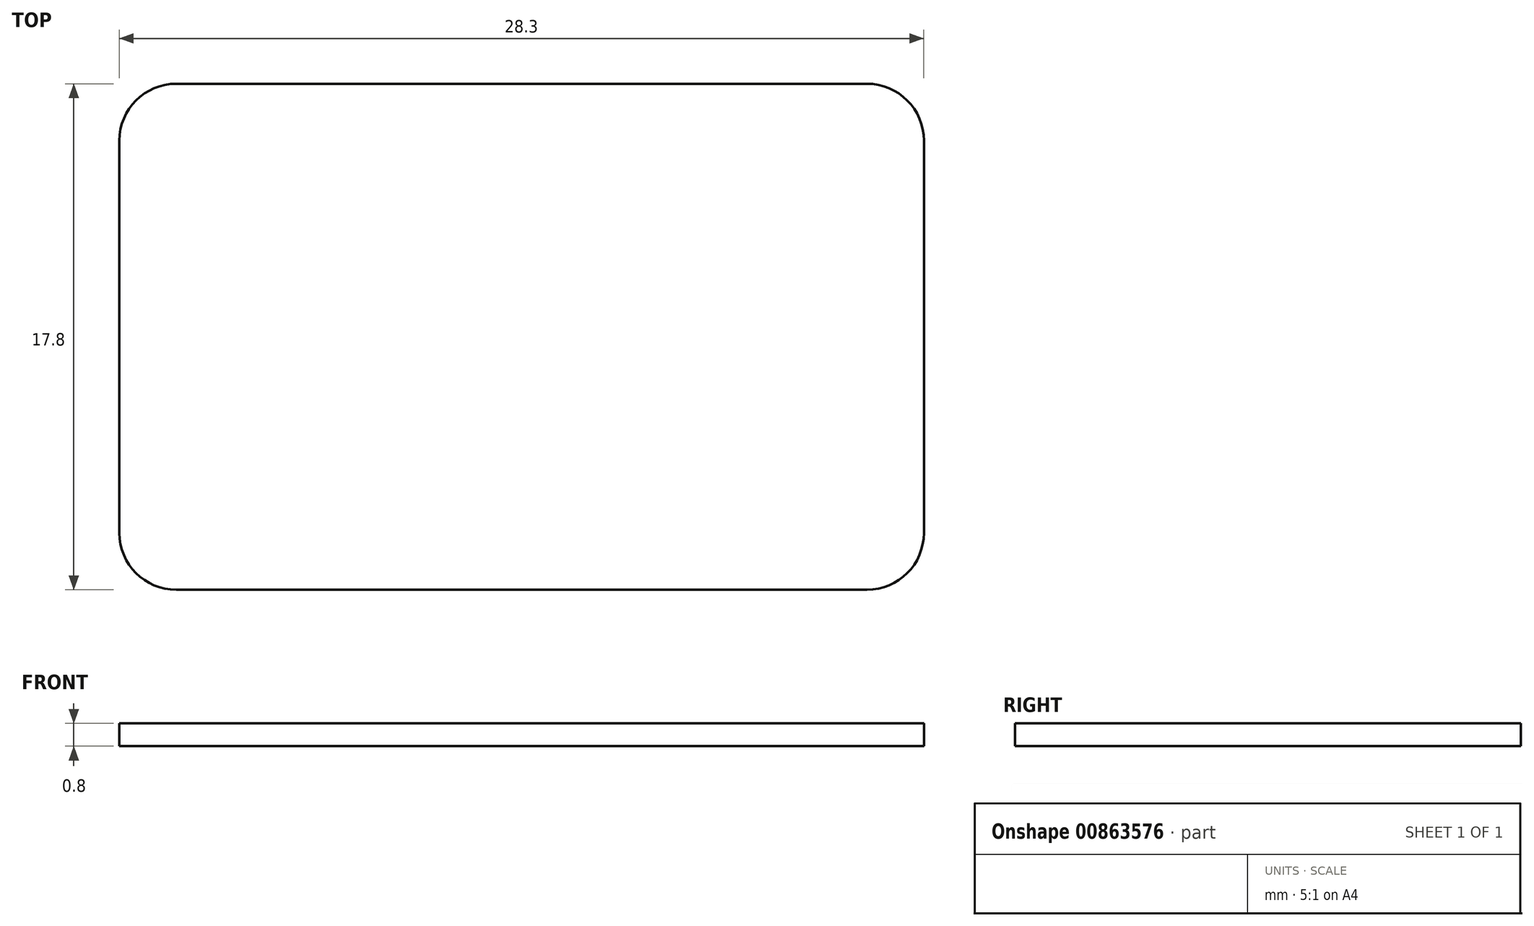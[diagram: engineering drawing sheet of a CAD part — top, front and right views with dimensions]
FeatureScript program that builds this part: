
annotation { "Feature Type Name" : "Feature", "Feature Type Description" : "" }
export const myFeature = defineFeature(function(context is Context, id is Id, definition is map)
    precondition{}
    {
        {
            var Q0;
            Q0=qCreatedBy(makeId("Top.planeOp"),FACE);
            var sketch = newSketch(context, id + "F0", { "sketchPlane" : qUnion([Q0])});
            skLineSegment(sketch, "E0.bottom", {"start": v(-21.54, 8.61) * mm, "end": v(2.76, 8.61) * mm});
            skLineSegment(sketch, "E0.top", {"start": v(-21.54, -9.19) * mm, "end": v(2.76, -9.19) * mm});
            skLineSegment(sketch, "E0.left", {"start": v(-23.54, 6.61) * mm, "end": v(-23.54, -7.19) * mm});
            skLineSegment(sketch, "E0.right", {"start": v(4.76, 6.61) * mm, "end": v(4.76, -7.19) * mm});
            skPoint(sketch, "E1.visualSharp", {"position": v(-23.54, 8.61) * mm});
            skArc(sketch, "E1.filletArc", {"start": v(-21.54, 8.61) * mm, "mid": v(-22.95, 8.03) * mm, "end": v(-23.54, 6.61) * mm});
            skPoint(sketch, "E2.visualSharp", {"position": v(4.76, 8.61) * mm});
            skArc(sketch, "E2.filletArc", {"start": v(4.76, 6.61) * mm, "mid": v(4.18, 8.03) * mm, "end": v(2.76, 8.61) * mm});
            skPoint(sketch, "E3.visualSharp", {"position": v(-23.54, -9.19) * mm});
            skArc(sketch, "E3.filletArc", {"start": v(-23.54, -7.19) * mm, "mid": v(-22.95, -8.6) * mm, "end": v(-21.54, -9.19) * mm});
            skPoint(sketch, "E4.visualSharp", {"position": v(4.76, -9.19) * mm});
            skArc(sketch, "E4.filletArc", {"start": v(2.76, -9.19) * mm, "mid": v(4.18, -8.6) * mm, "end": v(4.76, -7.19) * mm});
            skSolve(sketch);
        }
        {
            var Q0;
            Q0=makeQuery(id+"F0.imprint","IMPRINT",FACE,{"disambiguationData":[TD([[makeQuery(id+"F0.imprint","IMPRINT",EDGE,{"derivedFrom":sQuery(id+"F0.wireOp",EDGE,"E0.bottom")}),-1.0]])]});
            extrude(context, id + "F1", {"entities" : qUnion([Q0]), "depth" : 0.8 * mm, "offsetDistance" : 25 * mm});
        }
    });
